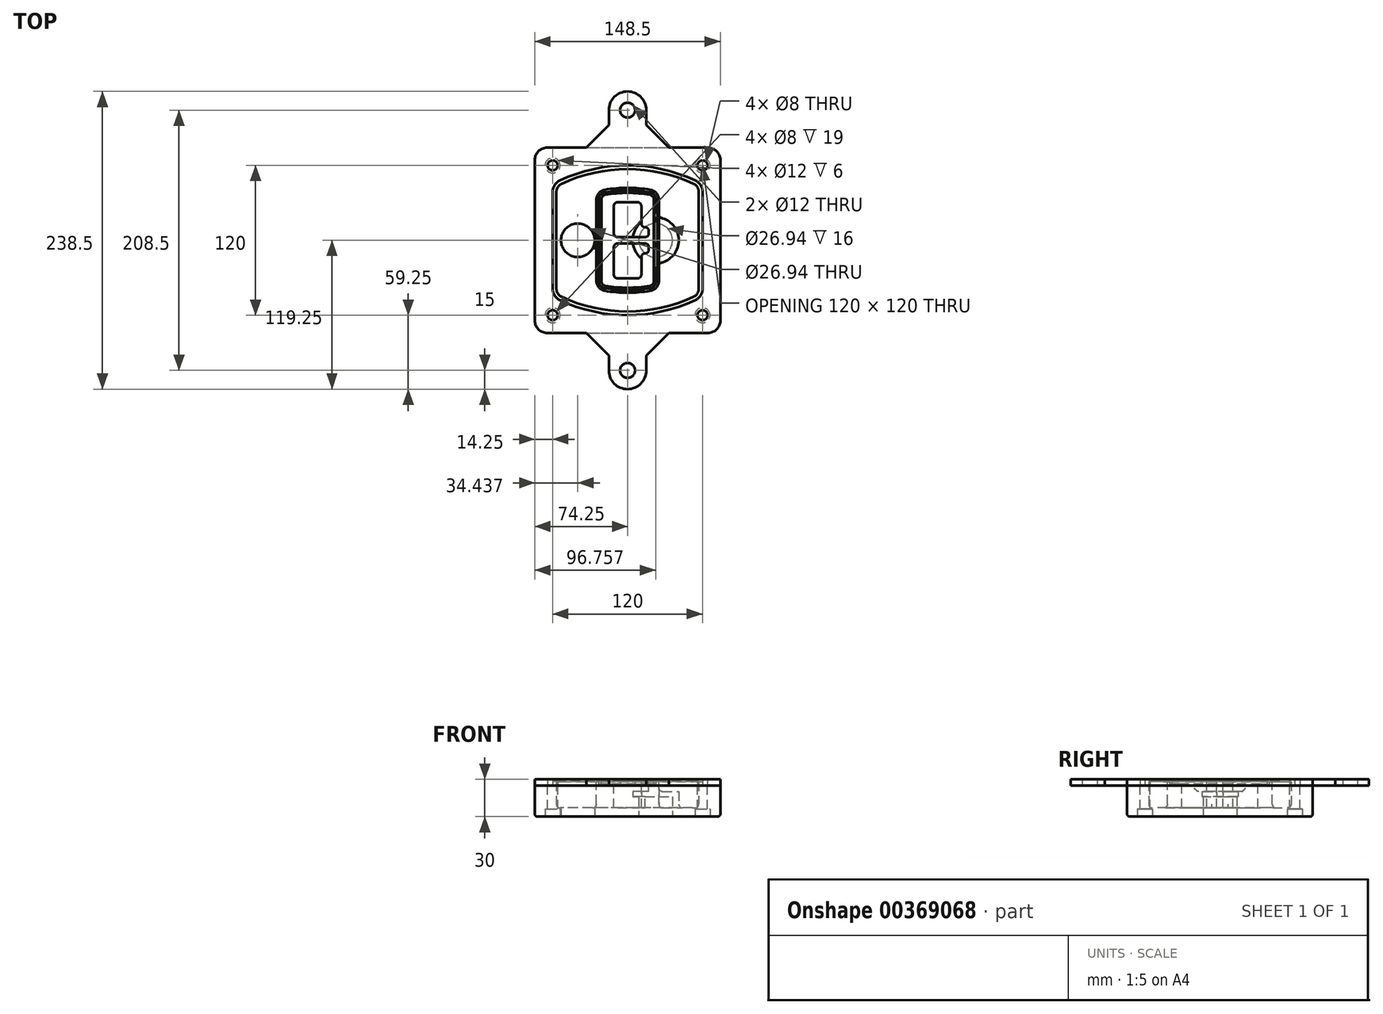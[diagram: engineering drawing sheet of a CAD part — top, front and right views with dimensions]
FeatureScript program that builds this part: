
annotation { "Feature Type Name" : "Feature", "Feature Type Description" : "" }
export const myFeature = defineFeature(function(context is Context, id is Id, definition is map)
    precondition{}
    {
        {
            var Q0;
            Q0=qCreatedBy(makeId("Top.planeOp"),FACE);
            var sketch = newSketch(context, id + "F0", { "sketchPlane" : qUnion([Q0])});
            skPoint(sketch, "E0.rect.middle", {"position": v(0, 0) * mm});
            skLineSegment(sketch, "E1.bottom", {"start": v(-64.25, -74.25) * mm, "end": v(64.25, -74.25) * mm});
            skLineSegment(sketch, "E1.top", {"start": v(-64.25, 74.25) * mm, "end": v(64.25, 74.25) * mm});
            skLineSegment(sketch, "E1.left", {"start": v(-74.25, -64.25) * mm, "end": v(-74.25, 64.25) * mm});
            skLineSegment(sketch, "E1.right", {"start": v(74.25, -64.25) * mm, "end": v(74.25, 64.25) * mm});
            skLineSegment(sketch, "E2", {"start": v(-74.25, 74.25) * mm, "end": v(74.25, -74.25) * mm, "construction": true});
            skLineSegment(sketch, "E3", {"start": v(74.25, 74.25) * mm, "end": v(-74.25, -74.25) * mm, "construction": true});
            skCircle(sketch, "E4", {"center": v(-60, 60) * mm, "radius": 4 * mm});
            skCircle(sketch, "E5", {"center": v(60, 60) * mm, "radius": 4 * mm});
            skCircle(sketch, "E6", {"center": v(60, -60) * mm, "radius": 4 * mm});
            skCircle(sketch, "E7", {"center": v(-60, -60) * mm, "radius": 4 * mm});
            skLineSegment(sketch, "E8", {"start": v(-60, 60) * mm, "end": v(60, 60) * mm, "construction": true});
            skLineSegment(sketch, "E9", {"start": v(60, 60) * mm, "end": v(60, -60) * mm, "construction": true});
            skLineSegment(sketch, "E10", {"start": v(60, -60) * mm, "end": v(-60, -60) * mm, "construction": true});
            skLineSegment(sketch, "E11", {"start": v(-60, -60) * mm, "end": v(-60, 60) * mm, "construction": true});
            skLineSegment(sketch, "E12", {"start": v(-60, 38.83) * mm, "end": v(-60, -38.83) * mm});
            skLineSegment(sketch, "E13", {"start": v(60, 38.83) * mm, "end": v(60, -38.83) * mm});
            skArc(sketch, "E14", {"start": v(54.26, 47.88) * mm, "mid": v(0, 60) * mm, "end": v(-54.26, 47.88) * mm});
            skArc(sketch, "E15", {"start": v(-54.26, -47.88) * mm, "mid": v(0, -60) * mm, "end": v(54.26, -47.88) * mm});
            skLineSegment(sketch, "E16", {"start": v(-60, 0) * mm, "end": v(60, 0) * mm, "construction": true});
            skPoint(sketch, "E17.visualSharp", {"position": v(-60, -45) * mm});
            skArc(sketch, "E17.filletArc", {"start": v(-60, -38.83) * mm, "mid": v(-58.44, -44.2) * mm, "end": v(-54.26, -47.88) * mm});
            skPoint(sketch, "E18.visualSharp", {"position": v(-60, 45) * mm});
            skArc(sketch, "E18.filletArc", {"start": v(-54.26, 47.88) * mm, "mid": v(-58.44, 44.2) * mm, "end": v(-60, 38.83) * mm});
            skPoint(sketch, "E19.visualSharp", {"position": v(60, 45) * mm});
            skArc(sketch, "E19.filletArc", {"start": v(60, 38.83) * mm, "mid": v(58.44, 44.2) * mm, "end": v(54.26, 47.88) * mm});
            skPoint(sketch, "E20.visualSharp", {"position": v(60, -45) * mm});
            skArc(sketch, "E20.filletArc", {"start": v(54.26, -47.88) * mm, "mid": v(58.44, -44.2) * mm, "end": v(60, -38.83) * mm});
            skPoint(sketch, "E21.visualSharp", {"position": v(-74.25, 74.25) * mm});
            skArc(sketch, "E21.filletArc", {"start": v(-64.25, 74.25) * mm, "mid": v(-71.32, 71.32) * mm, "end": v(-74.25, 64.25) * mm});
            skPoint(sketch, "E22.visualSharp", {"position": v(74.25, 74.25) * mm});
            skArc(sketch, "E22.filletArc", {"start": v(74.25, 64.25) * mm, "mid": v(71.32, 71.32) * mm, "end": v(64.25, 74.25) * mm});
            skPoint(sketch, "E23.visualSharp", {"position": v(74.25, -74.25) * mm});
            skArc(sketch, "E23.filletArc", {"start": v(64.25, -74.25) * mm, "mid": v(71.32, -71.32) * mm, "end": v(74.25, -64.25) * mm});
            skPoint(sketch, "E24.visualSharp", {"position": v(-74.25, -74.25) * mm});
            skArc(sketch, "E24.filletArc", {"start": v(-74.25, -64.25) * mm, "mid": v(-71.32, -71.32) * mm, "end": v(-64.25, -74.25) * mm});
            skArc(sketch, "E25.0", {"start": v(57, 38.83) * mm, "mid": v(55.9, 42.58) * mm, "end": v(52.98, 45.17) * mm});
            skLineSegment(sketch, "E25.1", {"start": v(57, 38.83) * mm, "end": v(57, -38.83) * mm});
            skArc(sketch, "E25.2", {"start": v(52.98, -45.17) * mm, "mid": v(55.9, -42.58) * mm, "end": v(57, -38.83) * mm});
            skArc(sketch, "E25.3", {"start": v(-52.98, -45.17) * mm, "mid": v(0, -57) * mm, "end": v(52.98, -45.17) * mm});
            skArc(sketch, "E25.4", {"start": v(-57, -38.83) * mm, "mid": v(-55.9, -42.58) * mm, "end": v(-52.98, -45.17) * mm});
            skArc(sketch, "E25.5", {"start": v(52.98, 45.17) * mm, "mid": v(0, 57) * mm, "end": v(-52.98, 45.17) * mm});
            skLineSegment(sketch, "E25.6", {"start": v(-57, 38.83) * mm, "end": v(-57, -38.83) * mm});
            skArc(sketch, "E25.7", {"start": v(-52.98, 45.17) * mm, "mid": v(-55.9, 42.58) * mm, "end": v(-57, 38.83) * mm});
            skArc(sketch, "E26.0", {"start": v(-55.96, 51.5) * mm, "mid": v(-61.82, 46.33) * mm, "end": v(-64, 38.83) * mm});
            skArc(sketch, "E26.1", {"start": v(55.96, 51.5) * mm, "mid": v(0, 64) * mm, "end": v(-55.96, 51.5) * mm});
            skArc(sketch, "E26.2", {"start": v(64, 38.83) * mm, "mid": v(61.82, 46.33) * mm, "end": v(55.96, 51.5) * mm});
            skLineSegment(sketch, "E26.3", {"start": v(64, 38.83) * mm, "end": v(64, -38.83) * mm});
            skArc(sketch, "E26.4", {"start": v(55.96, -51.5) * mm, "mid": v(61.82, -46.33) * mm, "end": v(64, -38.83) * mm});
            skLineSegment(sketch, "E26.5", {"start": v(-64, 38.83) * mm, "end": v(-64, -38.83) * mm});
            skArc(sketch, "E26.6", {"start": v(-55.96, -51.5) * mm, "mid": v(0, -64) * mm, "end": v(55.96, -51.5) * mm});
            skArc(sketch, "E26.7", {"start": v(-64, -38.83) * mm, "mid": v(-61.82, -46.33) * mm, "end": v(-55.96, -51.5) * mm});
            skSolve(sketch);
        }
        {
            var Q0;
            Q0=makeQuery(id+"F0.imprint","IMPRINT",FACE,{"disambiguationData":[TD([[makeQuery(id+"F0.imprint","IMPRINT",EDGE,{"derivedFrom":sQuery(id+"F0.wireOp",EDGE,"E1.bottom")}),1.0]])]});
            var Q1;
            Q1=makeQuery(id+"F0.imprint","IMPRINT",FACE,{"disambiguationData":[TD([[makeQuery(id+"F0.imprint","IMPRINT",EDGE,{"derivedFrom":sQuery(id+"F0.wireOp",EDGE,"E12")}),1.0]])]});
            var Q2;
            Q2=makeQuery(id+"F0.imprint","IMPRINT",FACE,{"disambiguationData":[TD([[makeQuery(id+"F0.imprint","IMPRINT",EDGE,{"derivedFrom":sQuery(id+"F0.wireOp",EDGE,"E25.0")}),1.0]])]});
            var Q3;
            Q3=makeQuery(id+"F0.imprint","IMPRINT",FACE,{"disambiguationData":[TD([[makeQuery(id+"F0.imprint","IMPRINT",EDGE,{"derivedFrom":sQuery(id+"F0.wireOp",EDGE,"E12")}),-1.0]])]});
            extrude(context, id + "F1", {"entities" : qUnion([Q0, Q1, Q2, Q3]), "oppositeDirection" : true, "depth" : 25 * mm});
        }
        {
            var Q0;
            Q0=makeQuery(id+"F0.imprint","IMPRINT",FACE,{"disambiguationData":[TD([[makeQuery(id+"F0.imprint","IMPRINT",EDGE,{"derivedFrom":sQuery(id+"F0.wireOp",EDGE,"E12")}),1.0]])]});
            extrude(context, id + "F2", {"entities" : qUnion([Q0]), "operationType" : NewBodyOperationType.ADD, "depth" : 3 * mm});
        }
        {
            var Q0;
            Q0=makeQuery(id+"F0.imprint","IMPRINT",FACE,{"disambiguationData":[TD([[makeQuery(id+"F0.imprint","IMPRINT",EDGE,{"derivedFrom":sQuery(id+"F0.wireOp",EDGE,"E25.0")}),1.0]])]});
            extrude(context, id + "F3", {"entities" : qUnion([Q0]), "operationType" : NewBodyOperationType.REMOVE, "oppositeDirection" : true, "depth" : 18 * mm});
        }
        {
            var Q0;
            Q0=makeQuery(id+"F2.opExtrude","CAP_FACE",FACE,{"disambiguationData":[OSD([sQuery(id+"F0.wireOp",EDGE,"E12"),sQuery(id+"F0.wireOp",EDGE,"E13"),sQuery(id+"F0.wireOp",EDGE,"E14"),sQuery(id+"F0.wireOp",EDGE,"E15"),sQuery(id+"F0.wireOp",EDGE,"E17.filletArc"),sQuery(id+"F0.wireOp",EDGE,"E18.filletArc"),sQuery(id+"F0.wireOp",EDGE,"E19.filletArc"),sQuery(id+"F0.wireOp",EDGE,"E20.filletArc"),sQuery(id+"F0.wireOp",EDGE,"E25.0"),sQuery(id+"F0.wireOp",EDGE,"E25.1"),sQuery(id+"F0.wireOp",EDGE,"E25.2"),sQuery(id+"F0.wireOp",EDGE,"E25.3"),sQuery(id+"F0.wireOp",EDGE,"E25.4"),sQuery(id+"F0.wireOp",EDGE,"E25.5"),sQuery(id+"F0.wireOp",EDGE,"E25.6"),sQuery(id+"F0.wireOp",EDGE,"E25.7")])],"isStart":false});
            var sketch = newSketch(context, id + "F4", { "sketchPlane" : qUnion([Q0])});
            skArc(sketch, "E27.0", {"start": v(-18.34, -40.45) * mm, "mid": v(0, -42) * mm, "end": v(18.34, -40.45) * mm});
            skArc(sketch, "E28.0", {"start": v(18.34, 40.45) * mm, "mid": v(0, 42) * mm, "end": v(-18.34, 40.45) * mm});
            skLineSegment(sketch, "E29", {"start": v(-25, 32.57) * mm, "end": v(-25, -32.57) * mm});
            skLineSegment(sketch, "E30", {"start": v(25, 32.57) * mm, "end": v(25, -32.57) * mm});
            skLineSegment(sketch, "E31", {"start": v(-25, 39.1) * mm, "end": v(25, 39.1) * mm, "construction": true});
            skLineSegment(sketch, "E32", {"start": v(-25, -39.1) * mm, "end": v(25, -39.1) * mm, "construction": true});
            skPoint(sketch, "E33.visualSharp", {"position": v(-25, 39.1) * mm});
            skArc(sketch, "E33.filletArc", {"start": v(-18.34, 40.45) * mm, "mid": v(-23.11, 37.73) * mm, "end": v(-25, 32.57) * mm});
            skPoint(sketch, "E34.visualSharp", {"position": v(25, 39.1) * mm});
            skArc(sketch, "E34.filletArc", {"start": v(25, 32.57) * mm, "mid": v(23.11, 37.73) * mm, "end": v(18.34, 40.45) * mm});
            skPoint(sketch, "E35.visualSharp", {"position": v(25, -39.1) * mm});
            skArc(sketch, "E35.filletArc", {"start": v(18.34, -40.45) * mm, "mid": v(23.11, -37.73) * mm, "end": v(25, -32.57) * mm});
            skPoint(sketch, "E36.visualSharp", {"position": v(-25, -39.1) * mm});
            skArc(sketch, "E36.filletArc", {"start": v(-25, -32.57) * mm, "mid": v(-23.11, -37.73) * mm, "end": v(-18.34, -40.45) * mm});
            skArc(sketch, "E37.0", {"start": v(52.98, 45.17) * mm, "mid": v(0, 57) * mm, "end": v(-52.98, 45.17) * mm});
            skArc(sketch, "E37.1", {"start": v(-52.98, 45.17) * mm, "mid": v(-55.9, 42.58) * mm, "end": v(-57, 38.83) * mm});
            skLineSegment(sketch, "E37.2", {"start": v(-57, 38.83) * mm, "end": v(-57, -38.83) * mm});
            skArc(sketch, "E37.3", {"start": v(-57, -38.83) * mm, "mid": v(-55.9, -42.58) * mm, "end": v(-52.98, -45.17) * mm});
            skArc(sketch, "E37.4", {"start": v(-52.98, -45.17) * mm, "mid": v(0, -57) * mm, "end": v(52.98, -45.17) * mm});
            skArc(sketch, "E37.5", {"start": v(52.98, -45.17) * mm, "mid": v(55.9, -42.58) * mm, "end": v(57, -38.83) * mm});
            skLineSegment(sketch, "E37.6", {"start": v(57, 38.83) * mm, "end": v(57, -38.83) * mm});
            skArc(sketch, "E37.7", {"start": v(57, 38.83) * mm, "mid": v(55.9, 42.58) * mm, "end": v(52.98, 45.17) * mm});
            skLineSegment(sketch, "E38.0", {"start": v(23, 32.57) * mm, "end": v(23, -32.57) * mm});
            skArc(sketch, "E38.1", {"start": v(18, -38.48) * mm, "mid": v(21.58, -36.44) * mm, "end": v(23, -32.57) * mm});
            skArc(sketch, "E38.2", {"start": v(-18, -38.48) * mm, "mid": v(0, -40) * mm, "end": v(18, -38.48) * mm});
            skArc(sketch, "E38.3", {"start": v(-23, -32.57) * mm, "mid": v(-21.58, -36.44) * mm, "end": v(-18, -38.48) * mm});
            skLineSegment(sketch, "E38.4", {"start": v(-23, 32.57) * mm, "end": v(-23, -32.57) * mm});
            skArc(sketch, "E38.5", {"start": v(23, 32.57) * mm, "mid": v(21.58, 36.44) * mm, "end": v(18, 38.48) * mm});
            skArc(sketch, "E38.6", {"start": v(-18, 38.48) * mm, "mid": v(-21.58, 36.44) * mm, "end": v(-23, 32.57) * mm});
            skArc(sketch, "E38.7", {"start": v(18, 38.48) * mm, "mid": v(0, 40) * mm, "end": v(-18, 38.48) * mm});
            skArc(sketch, "E39.0", {"start": v(21, 32.57) * mm, "mid": v(20.06, 35.15) * mm, "end": v(17.67, 36.5) * mm});
            skLineSegment(sketch, "E39.1", {"start": v(21, 32.57) * mm, "end": v(21, -32.57) * mm});
            skArc(sketch, "E39.2", {"start": v(17.67, -36.5) * mm, "mid": v(20.06, -35.15) * mm, "end": v(21, -32.57) * mm});
            skArc(sketch, "E39.3", {"start": v(-17.67, -36.5) * mm, "mid": v(0, -38) * mm, "end": v(17.67, -36.5) * mm});
            skArc(sketch, "E39.4", {"start": v(-21, -32.57) * mm, "mid": v(-20.06, -35.15) * mm, "end": v(-17.67, -36.5) * mm});
            skArc(sketch, "E39.5", {"start": v(17.67, 36.5) * mm, "mid": v(0, 38) * mm, "end": v(-17.67, 36.5) * mm});
            skLineSegment(sketch, "E39.6", {"start": v(-21, 32.57) * mm, "end": v(-21, -32.57) * mm});
            skArc(sketch, "E39.7", {"start": v(-17.67, 36.5) * mm, "mid": v(-20.06, 35.15) * mm, "end": v(-21, 32.57) * mm});
            skLineSegment(sketch, "E40", {"start": v(-25, 0) * mm, "end": v(25, 0) * mm, "construction": true});
            skLineSegment(sketch, "E41", {"start": v(-11, 5.5) * mm, "end": v(-11, 27.5) * mm});
            skLineSegment(sketch, "E42", {"start": v(-8, 30.5) * mm, "end": v(8, 30.5) * mm});
            skLineSegment(sketch, "E43", {"start": v(11, 27.5) * mm, "end": v(11, 13.5) * mm});
            skLineSegment(sketch, "E44", {"start": v(14, 10.5) * mm, "end": v(14, 10.5) * mm});
            skLineSegment(sketch, "E45", {"start": v(17, 7.5) * mm, "end": v(17, 5.5) * mm});
            skLineSegment(sketch, "E46", {"start": v(14, 2.5) * mm, "end": v(-8, 2.5) * mm});
            skPoint(sketch, "E47.visualSharp", {"position": v(-11, 30.5) * mm});
            skArc(sketch, "E47.filletArc", {"start": v(-8, 30.5) * mm, "mid": v(-10.12, 29.62) * mm, "end": v(-11, 27.5) * mm});
            skPoint(sketch, "E48.visualSharp", {"position": v(11, 30.5) * mm});
            skArc(sketch, "E48.filletArc", {"start": v(11, 27.5) * mm, "mid": v(10.12, 29.62) * mm, "end": v(8, 30.5) * mm});
            skPoint(sketch, "E49.visualSharp", {"position": v(11, 10.5) * mm});
            skArc(sketch, "E49.filletArc", {"start": v(11, 13.5) * mm, "mid": v(11.88, 11.38) * mm, "end": v(14, 10.5) * mm});
            skPoint(sketch, "E50.visualSharp", {"position": v(17, 10.5) * mm});
            skArc(sketch, "E50.filletArc", {"start": v(17, 7.5) * mm, "mid": v(16.12, 9.62) * mm, "end": v(14, 10.5) * mm});
            skPoint(sketch, "E51.visualSharp", {"position": v(17, 2.5) * mm});
            skArc(sketch, "E51.filletArc", {"start": v(14, 2.5) * mm, "mid": v(16.12, 3.38) * mm, "end": v(17, 5.5) * mm});
            skPoint(sketch, "E52.visualSharp", {"position": v(-11, 2.5) * mm});
            skArc(sketch, "E52.filletArc", {"start": v(-11, 5.5) * mm, "mid": v(-10.12, 3.38) * mm, "end": v(-8, 2.5) * mm});
            skLineSegment(sketch, "E53.0.MirrorCS", {"start": v(14, -2.5) * mm, "end": v(-8, -2.5) * mm});
            skArc(sketch, "E54.0.MirrorCS", {"start": v(-11, -5.5) * mm, "mid": v(-10.12, -3.38) * mm, "end": v(-8, -2.5) * mm});
            skLineSegment(sketch, "E55.0.MirrorCS", {"start": v(-11, -5.5) * mm, "end": v(-11, -27.5) * mm});
            skArc(sketch, "E56.0.MirrorCS", {"start": v(-8, -30.5) * mm, "mid": v(-10.12, -29.62) * mm, "end": v(-11, -27.5) * mm});
            skLineSegment(sketch, "E57.0.MirrorCS", {"start": v(-8, -30.5) * mm, "end": v(8, -30.5) * mm});
            skArc(sketch, "E58.0.MirrorCS", {"start": v(11, -27.5) * mm, "mid": v(10.12, -29.62) * mm, "end": v(8, -30.5) * mm});
            skLineSegment(sketch, "E59.0.MirrorCS", {"start": v(11, -27.5) * mm, "end": v(11, -13.5) * mm});
            skArc(sketch, "E60.0.MirrorCS", {"start": v(11, -13.5) * mm, "mid": v(11.88, -11.38) * mm, "end": v(14, -10.5) * mm});
            skArc(sketch, "E61.0.MirrorCS", {"start": v(17, -7.5) * mm, "mid": v(16.12, -9.62) * mm, "end": v(14, -10.5) * mm});
            skLineSegment(sketch, "E62.0.MirrorCS", {"start": v(17, -7.5) * mm, "end": v(17, -5.5) * mm});
            skArc(sketch, "E63.0.MirrorCS", {"start": v(14, -2.5) * mm, "mid": v(16.12, -3.38) * mm, "end": v(17, -5.5) * mm});
            skSolve(sketch);
        }
        {
            var Q0;
            Q0=makeQuery(id+"F4.imprint","IMPRINT",FACE,{"disambiguationData":[TD([[makeQuery(id+"F4.imprint","IMPRINT",EDGE,{"derivedFrom":sQuery(id+"F4.wireOp",EDGE,"E27.0")}),1.0]])]});
            var Q1;
            Q1=makeQuery(id+"F4.imprint","IMPRINT",FACE,{"disambiguationData":[TD([[makeQuery(id+"F4.imprint","IMPRINT",EDGE,{"derivedFrom":sQuery(id+"F4.wireOp",EDGE,"E38.0")}),-1.0]])]});
            var Q2;
            Q2=makeQuery(id+"F4.imprint","IMPRINT",FACE,{"disambiguationData":[TD([[makeQuery(id+"F4.imprint","IMPRINT",EDGE,{"derivedFrom":sQuery(id+"F4.wireOp",EDGE,"E39.0")}),1.0]])]});
            extrude(context, id + "F5", {"entities" : qUnion([Q0, Q1, Q2]), "operationType" : NewBodyOperationType.ADD, "endBound" : BoundingType.UP_TO_NEXT, "oppositeDirection" : true, "depth" : 25 * mm});
        }
        {
            var Q0;
            Q0=makeQuery(id+"F4.imprint","IMPRINT",FACE,{"disambiguationData":[TD([[makeQuery(id+"F4.imprint","IMPRINT",EDGE,{"derivedFrom":sQuery(id+"F4.wireOp",EDGE,"E38.0")}),-1.0]])]});
            extrude(context, id + "F6", {"entities" : qUnion([Q0]), "operationType" : NewBodyOperationType.REMOVE, "oppositeDirection" : true, "depth" : 2 * mm});
        }
        {
            var Q0;
            Q0=makeQuery(id+"F1.opExtrude","CAP_FACE",FACE,{"disambiguationData":[OSD([sQuery(id+"F0.wireOp",EDGE,"E1.bottom"),sQuery(id+"F0.wireOp",EDGE,"E1.top"),sQuery(id+"F0.wireOp",EDGE,"E1.left"),sQuery(id+"F0.wireOp",EDGE,"E1.right"),sQuery(id+"F0.wireOp",EDGE,"E4"),sQuery(id+"F0.wireOp",EDGE,"E5"),sQuery(id+"F0.wireOp",EDGE,"E6"),sQuery(id+"F0.wireOp",EDGE,"E7"),sQuery(id+"F0.wireOp",EDGE,"E21.filletArc"),sQuery(id+"F0.wireOp",EDGE,"E22.filletArc"),sQuery(id+"F0.wireOp",EDGE,"E23.filletArc"),sQuery(id+"F0.wireOp",EDGE,"E24.filletArc")])],"isStart":false});
            var sketch = newSketch(context, id + "F7", { "sketchPlane" : qUnion([Q0])});
            skCircle(sketch, "E64", {"center": v(22.5, 0) * mm, "radius": 13.47 * mm});
            skCircle(sketch, "E65", {"center": v(-39.81, 0) * mm, "radius": 13.47 * mm});
            skLineSegment(sketch, "E66", {"start": v(74.25, 0) * mm, "end": v(-74.25, 0) * mm});
            skCircle(sketch, "E67", {"center": v(22.5, 0) * mm, "radius": 18.47 * mm});
            skCircle(sketch, "E68", {"center": v(60, -60) * mm, "radius": 6 * mm});
            skCircle(sketch, "E69", {"center": v(-60, -60) * mm, "radius": 6 * mm});
            skCircle(sketch, "E70", {"center": v(-60, 60) * mm, "radius": 6 * mm});
            skCircle(sketch, "E71", {"center": v(60, 60) * mm, "radius": 6 * mm});
            skSolve(sketch);
        }
        {
            var Q0;
            {var subQ1=sQuery(id+"F7.wireOp",EDGE,"E66");var subQ4=sQuery(id+"F7.wireOp",EDGE,"E64");var subQ6=makeQuery(id+"F7.imprint","INTERSECT",VERTEX,{"disambiguationData":[OD(0.0)],"derivedFrom":[subQ4,subQ1]});Q0=makeQuery(id+"F7.imprint","IMPRINT",FACE,{"disambiguationData":[TD([[makeQuery(id+"F7.imprint","IMPRINT",EDGE,{"disambiguationData":[TD([[subQ6,-1.0]])],"derivedFrom":subQ4}),-1.0]])]});}
            var Q1;
            {var subQ0=sQuery(id+"F7.wireOp",EDGE,"E66");var subQ1=sQuery(id+"F7.wireOp",EDGE,"E64");var subQ3=makeQuery(id+"F7.imprint","INTERSECT",VERTEX,{"disambiguationData":[OD(0.0)],"derivedFrom":[subQ1,subQ0]});Q1=makeQuery(id+"F7.imprint","IMPRINT",FACE,{"disambiguationData":[TD([[makeQuery(id+"F7.imprint","IMPRINT",EDGE,{"disambiguationData":[TD([[subQ3,-1.0]])],"derivedFrom":subQ1}),1.0]])]});}
            var Q2;
            {var subQ0=sQuery(id+"F7.wireOp",EDGE,"E66");var subQ1=sQuery(id+"F7.wireOp",EDGE,"E64");var subQ3=makeQuery(id+"F7.imprint","INTERSECT",VERTEX,{"disambiguationData":[OD(0.0)],"derivedFrom":[subQ1,subQ0]});Q2=makeQuery(id+"F7.imprint","IMPRINT",FACE,{"disambiguationData":[TD([[makeQuery(id+"F7.imprint","IMPRINT",EDGE,{"disambiguationData":[TD([[subQ3,1.0]])],"derivedFrom":subQ1}),1.0]])]});}
            var Q3;
            {var subQ1=sQuery(id+"F7.wireOp",EDGE,"E66");var subQ4=sQuery(id+"F7.wireOp",EDGE,"E64");var subQ6=makeQuery(id+"F7.imprint","INTERSECT",VERTEX,{"disambiguationData":[OD(0.0)],"derivedFrom":[subQ4,subQ1]});Q3=makeQuery(id+"F7.imprint","IMPRINT",FACE,{"disambiguationData":[TD([[makeQuery(id+"F7.imprint","IMPRINT",EDGE,{"disambiguationData":[TD([[subQ6,1.0]])],"derivedFrom":subQ4}),-1.0]])]});}
            extrude(context, id + "F8", {"entities" : qUnion([Q0, Q1, Q2, Q3]), "operationType" : NewBodyOperationType.ADD, "oppositeDirection" : true, "depth" : 20 * mm});
        }
        {
            var Q0;
            {var subQ0=sQuery(id+"F7.wireOp",EDGE,"E66");var subQ1=sQuery(id+"F7.wireOp",EDGE,"E64");var subQ3=makeQuery(id+"F7.imprint","INTERSECT",VERTEX,{"disambiguationData":[OD(0.0)],"derivedFrom":[subQ1,subQ0]});Q0=makeQuery(id+"F7.imprint","IMPRINT",FACE,{"disambiguationData":[TD([[makeQuery(id+"F7.imprint","IMPRINT",EDGE,{"disambiguationData":[TD([[subQ3,-1.0]])],"derivedFrom":subQ1}),1.0]])]});}
            var Q1;
            {var subQ0=sQuery(id+"F7.wireOp",EDGE,"E66");var subQ1=sQuery(id+"F7.wireOp",EDGE,"E64");var subQ3=makeQuery(id+"F7.imprint","INTERSECT",VERTEX,{"disambiguationData":[OD(0.0)],"derivedFrom":[subQ1,subQ0]});Q1=makeQuery(id+"F7.imprint","IMPRINT",FACE,{"disambiguationData":[TD([[makeQuery(id+"F7.imprint","IMPRINT",EDGE,{"disambiguationData":[TD([[subQ3,1.0]])],"derivedFrom":subQ1}),1.0]])]});}
            extrude(context, id + "F9", {"entities" : qUnion([Q0, Q1]), "operationType" : NewBodyOperationType.REMOVE, "oppositeDirection" : true, "depth" : 16 * mm});
        }
        {
            var Q0;
            {var subQ0=sQuery(id+"F7.wireOp",EDGE,"E66");var subQ1=sQuery(id+"F7.wireOp",EDGE,"E65");var subQ3=makeQuery(id+"F7.imprint","INTERSECT",VERTEX,{"disambiguationData":[OD(0.0)],"derivedFrom":[subQ1,subQ0]});Q0=makeQuery(id+"F7.imprint","IMPRINT",FACE,{"disambiguationData":[TD([[makeQuery(id+"F7.imprint","IMPRINT",EDGE,{"disambiguationData":[TD([[subQ3,-1.0]])],"derivedFrom":subQ1}),1.0]])]});}
            var Q1;
            {var subQ0=sQuery(id+"F7.wireOp",EDGE,"E66");var subQ1=sQuery(id+"F7.wireOp",EDGE,"E65");var subQ3=makeQuery(id+"F7.imprint","INTERSECT",VERTEX,{"disambiguationData":[OD(0.0)],"derivedFrom":[subQ1,subQ0]});Q1=makeQuery(id+"F7.imprint","IMPRINT",FACE,{"disambiguationData":[TD([[makeQuery(id+"F7.imprint","IMPRINT",EDGE,{"disambiguationData":[TD([[subQ3,1.0]])],"derivedFrom":subQ1}),1.0]])]});}
            extrude(context, id + "F10", {"entities" : qUnion([Q0, Q1]), "operationType" : NewBodyOperationType.REMOVE, "oppositeDirection" : true, "depth" : 25 * mm});
        }
        {
            var Q0;
            Q0=makeQuery(id+"F7.imprint","IMPRINT",FACE,{"disambiguationData":[TD([[makeQuery(id+"F7.imprint","IMPRINT",EDGE,{"derivedFrom":sQuery(id+"F7.wireOp",EDGE,"E68")}),1.0]])]});
            var Q1;
            Q1=makeQuery(id+"F7.imprint","IMPRINT",FACE,{"disambiguationData":[TD([[makeQuery(id+"F7.imprint","IMPRINT",EDGE,{"derivedFrom":makeQuery(id+"F1.opExtrude","CAP_EDGE",EDGE,{"disambiguationData":[OSD([sQuery(id+"F0.wireOp",EDGE,"E5")])],"isStart":false})}),-1.0]])]});
            var Q2;
            Q2=makeQuery(id+"F7.imprint","IMPRINT",FACE,{"disambiguationData":[TD([[makeQuery(id+"F7.imprint","IMPRINT",EDGE,{"derivedFrom":sQuery(id+"F7.wireOp",EDGE,"E69")}),1.0]])]});
            var Q3;
            Q3=makeQuery(id+"F7.imprint","IMPRINT",FACE,{"disambiguationData":[TD([[makeQuery(id+"F7.imprint","IMPRINT",EDGE,{"derivedFrom":makeQuery(id+"F1.opExtrude","CAP_EDGE",EDGE,{"disambiguationData":[OSD([sQuery(id+"F0.wireOp",EDGE,"E4")])],"isStart":false})}),-1.0]])]});
            var Q4;
            Q4=makeQuery(id+"F7.imprint","IMPRINT",FACE,{"disambiguationData":[TD([[makeQuery(id+"F7.imprint","IMPRINT",EDGE,{"derivedFrom":sQuery(id+"F7.wireOp",EDGE,"E70")}),1.0]])]});
            var Q5;
            Q5=makeQuery(id+"F7.imprint","IMPRINT",FACE,{"disambiguationData":[TD([[makeQuery(id+"F7.imprint","IMPRINT",EDGE,{"derivedFrom":makeQuery(id+"F1.opExtrude","CAP_EDGE",EDGE,{"disambiguationData":[OSD([sQuery(id+"F0.wireOp",EDGE,"E7")])],"isStart":false})}),-1.0]])]});
            var Q6;
            Q6=makeQuery(id+"F7.imprint","IMPRINT",FACE,{"disambiguationData":[TD([[makeQuery(id+"F7.imprint","IMPRINT",EDGE,{"derivedFrom":sQuery(id+"F7.wireOp",EDGE,"E71")}),1.0]])]});
            var Q7;
            Q7=makeQuery(id+"F7.imprint","IMPRINT",FACE,{"disambiguationData":[TD([[makeQuery(id+"F7.imprint","IMPRINT",EDGE,{"derivedFrom":makeQuery(id+"F1.opExtrude","CAP_EDGE",EDGE,{"disambiguationData":[OSD([sQuery(id+"F0.wireOp",EDGE,"E6")])],"isStart":false})}),-1.0]])]});
            extrude(context, id + "F11", {"entities" : qUnion([Q0, Q1, Q2, Q3, Q4, Q5, Q6, Q7]), "operationType" : NewBodyOperationType.REMOVE, "oppositeDirection" : true, "depth" : 6 * mm});
        }
        {
            var Q0;
            Q0=makeQuery(id+"F9.boolean.opBoolean","COPY",FACE,{"derivedFrom":makeQuery(id+"F9.opExtrude","CAP_FACE",FACE,{"disambiguationData":[OSD([sQuery(id+"F7.wireOp",EDGE,"E64")])],"isStart":false})});
            var sketch = newSketch(context, id + "F12", { "sketchPlane" : qUnion([Q0])});
            skArc(sketch, "E72.0", {"start": v(11, 14.45) * mm, "mid": v(6.45, 9.13) * mm, "end": v(4.2, 2.5) * mm});
            skArc(sketch, "E72.1", {"start": v(4.2, -2.5) * mm, "mid": v(6.45, -9.13) * mm, "end": v(11, -14.45) * mm});
            skLineSegment(sketch, "E73", {"start": v(4.2, -2.5) * mm, "end": v(14, -2.5) * mm});
            skLineSegment(sketch, "E74.0", {"start": v(14, 2.5) * mm, "end": v(4.2, 2.5) * mm});
            skArc(sketch, "E74.1", {"start": v(14, 2.5) * mm, "mid": v(16.12, 3.38) * mm, "end": v(17, 5.5) * mm});
            skLineSegment(sketch, "E74.2", {"start": v(17, 7.5) * mm, "end": v(17, 5.5) * mm});
            skArc(sketch, "E74.3", {"start": v(17, 7.5) * mm, "mid": v(16.12, 9.62) * mm, "end": v(14, 10.5) * mm});
            skArc(sketch, "E74.4", {"start": v(11, 13.5) * mm, "mid": v(11.88, 11.38) * mm, "end": v(14, 10.5) * mm});
            skLineSegment(sketch, "E74.5", {"start": v(11, 14.45) * mm, "end": v(11, 13.5) * mm});
            skLineSegment(sketch, "E74.7", {"start": v(14, -2.5) * mm, "end": v(4.2, -2.5) * mm});
            skArc(sketch, "E74.8", {"start": v(14, -2.5) * mm, "mid": v(16.12, -3.38) * mm, "end": v(17, -5.5) * mm});
            skLineSegment(sketch, "E74.9", {"start": v(17, -7.5) * mm, "end": v(17, -5.5) * mm});
            skArc(sketch, "E74.10", {"start": v(17, -7.5) * mm, "mid": v(16.12, -9.62) * mm, "end": v(14, -10.5) * mm});
            skArc(sketch, "E74.11", {"start": v(11, -13.5) * mm, "mid": v(11.88, -11.38) * mm, "end": v(14, -10.5) * mm});
            skLineSegment(sketch, "E74.12", {"start": v(11, -14.45) * mm, "end": v(11, -13.5) * mm});
            skPoint(sketch, "E75.orphan", {"position": v(11, -27.5) * mm});
            skPoint(sketch, "E76.orphan", {"position": v(-8, -2.5) * mm});
            skPoint(sketch, "E77.orphan", {"position": v(-8, 2.5) * mm});
            skPoint(sketch, "E78.orphan", {"position": v(11, 27.5) * mm});
            skSolve(sketch);
        }
        {
            var Q0;
            {var subQ7=sQuery(id+"F12.wireOp",EDGE,"E72.0");var subQ14=sQuery(id+"F12.wireOp",EDGE,"E72.1");var subQ16=sQuery(id+"F12.wireOp",EDGE,"E74.1");var subQ18=sQuery(id+"F12.wireOp",EDGE,"E74.8");Q0=qUnion([makeQuery(id+"F12.imprint","IMPRINT",FACE,{"disambiguationData":[TD([[makeQuery(id+"F12.imprint","IMPRINT",EDGE,{"derivedFrom":subQ7}),1.0]])]}),makeQuery(id+"F12.imprint","IMPRINT",FACE,{"disambiguationData":[TD([[makeQuery(id+"F12.imprint","IMPRINT",EDGE,{"derivedFrom":subQ14}),1.0]])]}),makeQuery(id+"F12.imprint","IMPRINT",FACE,{"disambiguationData":[TD([[makeQuery(id+"F12.imprint","IMPRINT",EDGE,{"derivedFrom":subQ16}),1.0]])]}),makeQuery(id+"F12.imprint","IMPRINT",FACE,{"disambiguationData":[TD([[makeQuery(id+"F12.imprint","IMPRINT",EDGE,{"derivedFrom":subQ18}),-1.0]])]})]);}
            var Q1;
            Q1=makeQuery(id+"F5.boolean.opBoolean","SPLIT",FACE,{"disambiguationData":[TD([makeQuery(id+"F5.opExtrude","SWEPT_FACE",FACE,{"disambiguationData":[OSD([sQuery(id+"F4.wireOp",EDGE,"E41")])]})])],"derivedFrom":makeQuery(id+"F3.boolean.opBoolean","COPY",FACE,{"derivedFrom":makeQuery(id+"F3.opExtrude","CAP_FACE",FACE,{"disambiguationData":[OSD([sQuery(id+"F0.wireOp",EDGE,"E25.0"),sQuery(id+"F0.wireOp",EDGE,"E25.1"),sQuery(id+"F0.wireOp",EDGE,"E25.2"),sQuery(id+"F0.wireOp",EDGE,"E25.3"),sQuery(id+"F0.wireOp",EDGE,"E25.4"),sQuery(id+"F0.wireOp",EDGE,"E25.5"),sQuery(id+"F0.wireOp",EDGE,"E25.6"),sQuery(id+"F0.wireOp",EDGE,"E25.7")])],"isStart":false})})});
            extrude(context, id + "F13", {"entities" : qUnion([Q0]), "operationType" : NewBodyOperationType.REMOVE, "endBound" : BoundingType.UP_TO_SURFACE, "endBoundEntityFace" : qUnion([Q1]), "depth" : 25 * mm});
        }
        {
            var Q0;
            Q0=makeQuery(id+"F3.boolean.opBoolean","COPY",EDGE,{"derivedFrom":makeQuery(id+"F3.opExtrude","CAP_EDGE",EDGE,{"disambiguationData":[OSD([sQuery(id+"F0.wireOp",EDGE,"E25.6")])],"isStart":false})});
            var Q1;
            Q1=makeQuery(id+"F8.boolean.opBoolean","INTERSECT",EDGE,{"derivedFrom":[makeQuery(id+"F5.opExtrude","SWEPT_FACE",FACE,{"disambiguationData":[OSD([sQuery(id+"F4.wireOp",EDGE,"E30")])]}),makeQuery(id+"F8.opExtrude","CAP_FACE",FACE,{"disambiguationData":[OSD([sQuery(id+"F7.wireOp",EDGE,"E67")])],"isStart":false})]});
            var Q2;
            Q2=makeQuery(id+"F8.boolean.opBoolean","INTERSECT",EDGE,{"disambiguationData":[OD(1.0)],"derivedFrom":[makeQuery(id+"F5.opExtrude","SWEPT_FACE",FACE,{"disambiguationData":[OSD([sQuery(id+"F4.wireOp",EDGE,"E30")])]}),makeQuery(id+"F8.opExtrude","SWEPT_FACE",FACE,{"disambiguationData":[OSD([sQuery(id+"F7.wireOp",EDGE,"E67")])]})]});
            var Q3;
            {var subQ0=sQuery(id+"F4.wireOp",EDGE,"E30");Q3=makeQuery(id+"F8.boolean.opBoolean","SPLIT",EDGE,{"disambiguationData":[TD([makeQuery(id+"F5.opExtrude","SWEPT_FACE",FACE,{"disambiguationData":[OSD([sQuery(id+"F4.wireOp",EDGE,"E35.filletArc")])]})])],"derivedFrom":makeQuery(id+"F5.opExtrude","CAP_EDGE",EDGE,{"disambiguationData":[OSD([subQ0])],"isStart":false})});}
            var Q4;
            {var subQ0=sQuery(id+"F0.wireOp",EDGE,"E25.7");var subQ1=sQuery(id+"F0.wireOp",EDGE,"E25.1");var subQ2=sQuery(id+"F0.wireOp",EDGE,"E25.6");var subQ3=sQuery(id+"F0.wireOp",EDGE,"E25.5");var subQ4=sQuery(id+"F0.wireOp",EDGE,"E25.4");var subQ5=sQuery(id+"F0.wireOp",EDGE,"E25.0");var subQ6=sQuery(id+"F0.wireOp",EDGE,"E25.2");var subQ7=sQuery(id+"F0.wireOp",EDGE,"E25.3");Q4=makeQuery(id+"F8.boolean.opBoolean","INTERSECT",EDGE,{"derivedFrom":[makeQuery(id+"F5.boolean.opBoolean","SPLIT",FACE,{"disambiguationData":[TD([makeQuery(id+"F2.opExtrude","SWEPT_FACE",FACE,{"disambiguationData":[OSD([subQ5])]})])],"derivedFrom":makeQuery(id+"F3.boolean.opBoolean","COPY",FACE,{"derivedFrom":makeQuery(id+"F3.opExtrude","CAP_FACE",FACE,{"disambiguationData":[OSD([subQ5,subQ1,subQ6,subQ7,subQ4,subQ3,subQ2,subQ0])],"isStart":false})})}),makeQuery(id+"F8.opExtrude","SWEPT_FACE",FACE,{"disambiguationData":[OSD([sQuery(id+"F7.wireOp",EDGE,"E67")])]})]});}
            var Q5;
            Q5=makeQuery(id+"F8.boolean.opBoolean","INTERSECT",EDGE,{"disambiguationData":[OD(0.0)],"derivedFrom":[makeQuery(id+"F5.opExtrude","SWEPT_FACE",FACE,{"disambiguationData":[OSD([sQuery(id+"F4.wireOp",EDGE,"E30")])]}),makeQuery(id+"F8.opExtrude","SWEPT_FACE",FACE,{"disambiguationData":[OSD([sQuery(id+"F7.wireOp",EDGE,"E67")])]})]});
            fillet(context, id + "F14", {"entities" : qUnion([Q0, Q1, Q2, Q3, Q4, Q5]), "radius" : 3 * mm, "tangentPropagation" : true, "allowEdgeOverflow" : false});
        }
        {
            var Q0;
            Q0=makeQuery(id+"F1.opExtrude","CAP_EDGE",EDGE,{"disambiguationData":[OSD([sQuery(id+"F0.wireOp",EDGE,"E1.bottom")])],"isStart":false});
            fillet(context, id + "F15", {"entities" : qUnion([Q0]), "radius" : 2 * mm, "tangentPropagation" : true, "allowEdgeOverflow" : false});
        }
        {
            var Q0;
            {var subQ0=sQuery(id+"F0.wireOp",EDGE,"E21.filletArc");var subQ1=sQuery(id+"F0.wireOp",EDGE,"E7");var subQ2=sQuery(id+"F0.wireOp",EDGE,"E6");var subQ3=sQuery(id+"F0.wireOp",EDGE,"E5");var subQ4=sQuery(id+"F0.wireOp",EDGE,"E4");var subQ5=sQuery(id+"F0.wireOp",EDGE,"E22.filletArc");var subQ6=sQuery(id+"F0.wireOp",EDGE,"E1.bottom");var subQ7=sQuery(id+"F0.wireOp",EDGE,"E1.right");var subQ8=sQuery(id+"F0.wireOp",EDGE,"E1.top");var subQ9=sQuery(id+"F0.wireOp",EDGE,"E1.left");var subQ10=sQuery(id+"F0.wireOp",EDGE,"E23.filletArc");var subQ11=sQuery(id+"F0.wireOp",EDGE,"E24.filletArc");Q0=makeQuery(id+"F2.boolean.opBoolean","SPLIT",FACE,{"disambiguationData":[TD([makeQuery(id+"F1.opExtrude","SWEPT_FACE",FACE,{"disambiguationData":[OSD([subQ6])]})])],"derivedFrom":makeQuery(id+"F1.opExtrude","CAP_FACE",FACE,{"disambiguationData":[OSD([subQ6,subQ8,subQ9,subQ7,subQ4,subQ3,subQ2,subQ1,subQ0,subQ5,subQ10,subQ11])],"isStart":true})});}
            var sketch = newSketch(context, id + "F16", { "sketchPlane" : qUnion([Q0])});
            skLineSegment(sketch, "E79", {"start": v(0, 74.25) * mm, "end": v(0, 104.25) * mm, "construction": true});
            skCircle(sketch, "E80", {"center": v(0, 104.25) * mm, "radius": 6 * mm});
            skLineSegment(sketch, "E81", {"start": v(-15, 104.25) * mm, "end": v(-15, 92.25) * mm});
            skLineSegment(sketch, "E82", {"start": v(15, 104.25) * mm, "end": v(15, 92.25) * mm});
            skArc(sketch, "E83", {"start": v(15, 104.25) * mm, "mid": v(0, 119.25) * mm, "end": v(-15, 104.25) * mm});
            skLineSegment(sketch, "E84", {"start": v(-15, 92.25) * mm, "end": v(-33, 74.25) * mm});
            skLineSegment(sketch, "E85", {"start": v(15, 92.25) * mm, "end": v(33, 74.25) * mm});
            skLineSegment(sketch, "E86.MirrorCS", {"start": v(-15, -92.25) * mm, "end": v(-33, -74.25) * mm});
            skLineSegment(sketch, "E87.MirrorCS", {"start": v(-15, -104.25) * mm, "end": v(-15, -92.25) * mm});
            skArc(sketch, "E88.MirrorCS", {"start": v(15, -104.25) * mm, "mid": v(0, -119.25) * mm, "end": v(-15, -104.25) * mm});
            skCircle(sketch, "E89.MirrorC", {"center": v(0, -104.25) * mm, "radius": 6 * mm});
            skLineSegment(sketch, "E90.MirrorCS", {"start": v(0, -74.25) * mm, "end": v(0, -104.25) * mm, "construction": true});
            skLineSegment(sketch, "E91.MirrorCS", {"start": v(15, -92.25) * mm, "end": v(33, -74.25) * mm});
            skLineSegment(sketch, "E92.MirrorCS", {"start": v(15, -104.25) * mm, "end": v(15, -92.25) * mm});
            skSolve(sketch);
        }
        {
            var Q0;
            Q0=makeQuery(id+"F16.imprint","IMPRINT",FACE,{"disambiguationData":[TD([[makeQuery(id+"F16.imprint","IMPRINT",EDGE,{"derivedFrom":makeQuery(id+"F1.opExtrude","CAP_EDGE",EDGE,{"disambiguationData":[OSD([sQuery(id+"F0.wireOp",EDGE,"E1.left")])],"isStart":true})}),-1.0]])]});
            var Q1;
            Q1=makeQuery(id+"F16.imprint","IMPRINT",FACE,{"disambiguationData":[TD([[makeQuery(id+"F16.imprint","IMPRINT",EDGE,{"derivedFrom":sQuery(id+"F16.wireOp",EDGE,"E80")}),-1.0]])]});
            var Q2;
            {var subQ0=sQuery(id+"F16.wireOp",EDGE,"E86.MirrorCS");Q2=makeQuery(id+"F16.imprint","IMPRINT",FACE,{"disambiguationData":[TD([[makeQuery(id+"F16.imprint","IMPRINT",EDGE,{"derivedFrom":subQ0}),-1.0]])]});}
            extrude(context, id + "F17", {"entities" : qUnion([Q0, Q1, Q2]), "depth" : 5 * mm});
        }
    });
